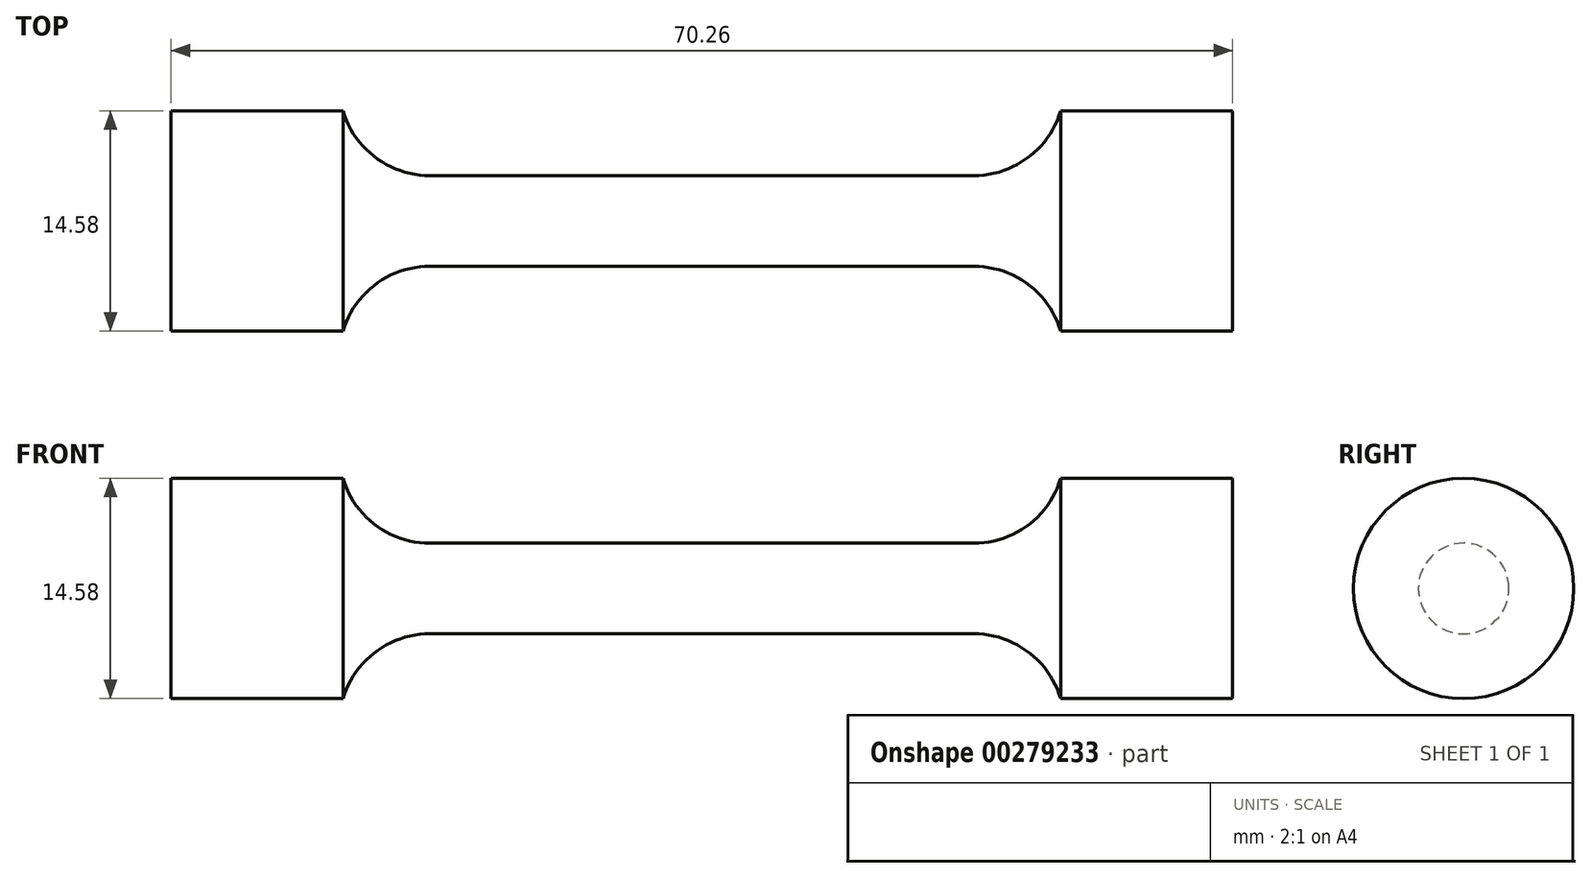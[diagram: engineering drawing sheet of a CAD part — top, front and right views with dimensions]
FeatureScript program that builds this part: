
annotation { "Feature Type Name" : "Feature", "Feature Type Description" : "" }
export const myFeature = defineFeature(function(context is Context, id is Id, definition is map)
    precondition{}
    {
        {
            var Q0;
            Q0=qCreatedBy(makeId("Front.planeOp"),FACE);
            var sketch = newSketch(context, id + "F0", { "sketchPlane" : qUnion([Q0])});
            skLineSegment(sketch, "E0", {"start": v(0, 3) * mm, "end": v(18, 3) * mm});
            skArc(sketch, "E1", {"start": v(18, 3) * mm, "mid": v(21.59, 4.2) * mm, "end": v(23.75, 7.29) * mm});
            skLineSegment(sketch, "E2", {"start": v(23.75, 7.29) * mm, "end": v(35.13, 7.29) * mm});
            skLineSegment(sketch, "E3", {"start": v(35.13, 7.29) * mm, "end": v(35.13, 0) * mm});
            skLineSegment(sketch, "E4.MirrorCS", {"start": v(0, 3) * mm, "end": v(-18, 3) * mm});
            skLineSegment(sketch, "E5.MirrorCS", {"start": v(-35.13, 7.29) * mm, "end": v(-35.13, 0) * mm});
            skLineSegment(sketch, "E6.MirrorCS", {"start": v(-23.75, 7.29) * mm, "end": v(-35.13, 7.29) * mm});
            skArc(sketch, "E7.MirrorCS", {"start": v(-18, 3) * mm, "mid": v(-21.59, 4.2) * mm, "end": v(-23.75, 7.29) * mm});
            skLineSegment(sketch, "E8", {"start": v(-35.13, 0) * mm, "end": v(35.13, 0) * mm});
            skSolve(sketch);
        }
        {
            var Q0;
            Q0=makeQuery(id+"F0.imprint","IMPRINT",FACE,{"disambiguationData":[TD([[makeQuery(id+"F0.imprint","IMPRINT",EDGE,{"derivedFrom":sQuery(id+"F0.wireOp",EDGE,"E0")}),-1.0]])]});
            var Q1;
            Q1=sQuery(id+"F0.wireOp",EDGE,"E8");
            revolve(context, id + "F1", {"entities" : qUnion([Q0]), "axis" : qUnion([Q1]), "revolveType" : RevolveType.FULL});
        }
    });
